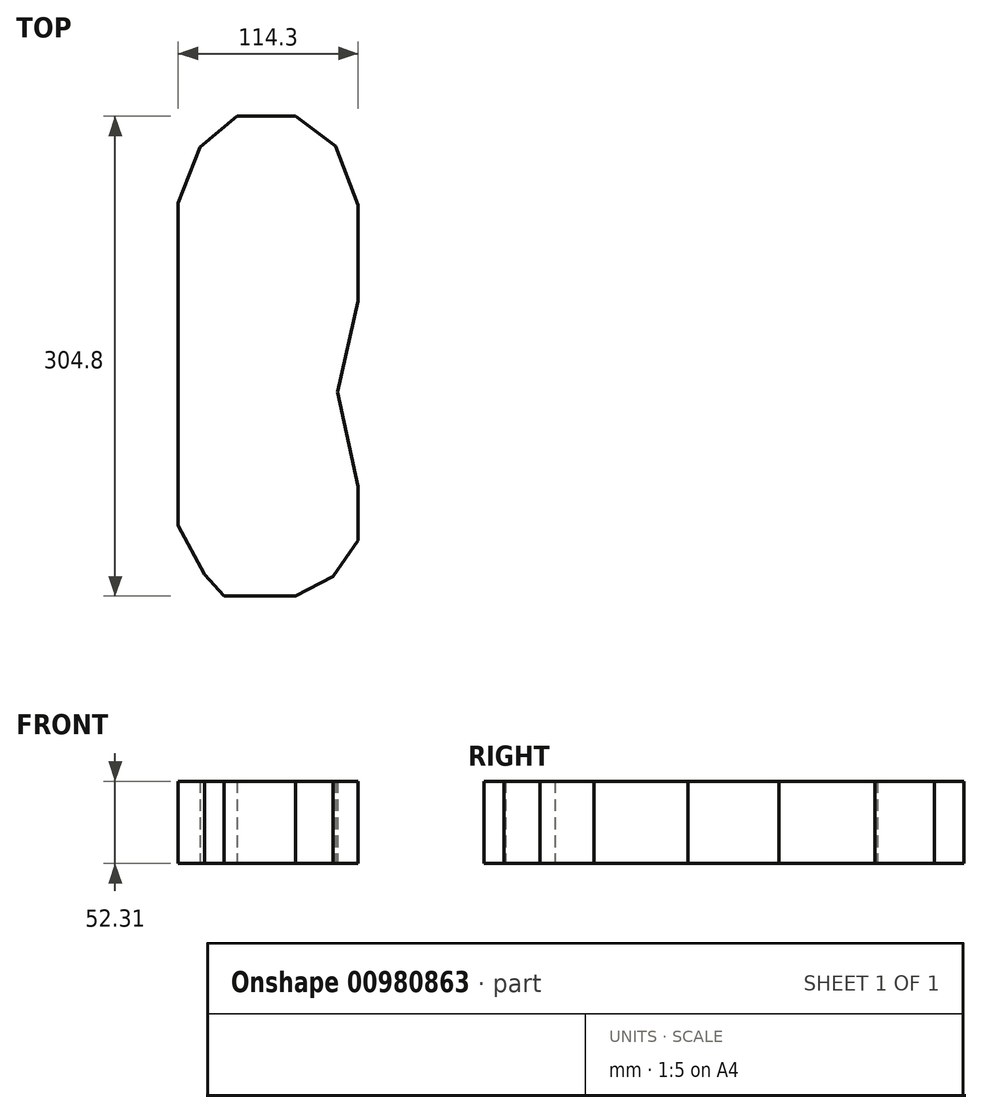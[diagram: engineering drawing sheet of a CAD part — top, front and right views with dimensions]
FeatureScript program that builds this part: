
annotation { "Feature Type Name" : "Feature", "Feature Type Description" : "" }
export const myFeature = defineFeature(function(context is Context, id is Id, definition is map)
    precondition{}
    {
        {
            var Q0;
            Q0=qCreatedBy(makeId("Top.planeOp"),FACE);
            var sketch = newSketch(context, id + "F0", { "sketchPlane" : qUnion([Q0])});
            skLineSegment(sketch, "E0", {"start": v(0, 0) * mm, "end": v(-114.3, 0) * mm});
            skLineSegment(sketch, "E1", {"start": v(-114.3, 304.8) * mm, "end": v(-114.3, 0) * mm});
            skLineSegment(sketch, "E2", {"start": v(0, 304.8) * mm, "end": v(0, 0) * mm});
            skLineSegment(sketch, "E3", {"start": v(-114.3, 304.8) * mm, "end": v(0, 304.8) * mm});
            skLineSegment(sketch, "E4", {"start": v(0, 187.34) * mm, "end": v(0, 69.7) * mm});
            skLineSegment(sketch, "E5", {"start": v(0, 248.35) * mm, "end": v(-14.43, 286.04) * mm});
            skLineSegment(sketch, "E6", {"start": v(-14.43, 286.04) * mm, "end": v(-39.67, 304.8) * mm});
            skLineSegment(sketch, "E7", {"start": v(-39.67, 304.8) * mm, "end": v(-77, 304.8) * mm});
            skLineSegment(sketch, "E8", {"start": v(-77, 304.8) * mm, "end": v(-100.47, 285.33) * mm});
            skLineSegment(sketch, "E9", {"start": v(-100.47, 285.33) * mm, "end": v(-114.3, 249.77) * mm});
            skLineSegment(sketch, "E10", {"start": v(0, 69.7) * mm, "end": v(-13, 129.59) * mm});
            skLineSegment(sketch, "E11", {"start": v(-13, 129.59) * mm, "end": v(0, 187.34) * mm});
            skLineSegment(sketch, "E12", {"start": v(0, 35.36) * mm, "end": v(-15.85, 12.6) * mm});
            skLineSegment(sketch, "E13", {"start": v(-15.85, 12.6) * mm, "end": v(-39.67, 0) * mm});
            skLineSegment(sketch, "E14", {"start": v(-39.67, 0) * mm, "end": v(-85.18, 0) * mm});
            skLineSegment(sketch, "E15", {"start": v(-85.18, 0) * mm, "end": v(-97.63, 13.68) * mm});
            skLineSegment(sketch, "E16", {"start": v(-97.63, 13.68) * mm, "end": v(-114.3, 44.97) * mm});
            skSolve(sketch);
        }
        {
            var Q0;
            {var subQ7=sQuery(id+"F0.wireOp",EDGE,"E5");Q0=makeQuery(id+"F0.imprint","IMPRINT",FACE,{"disambiguationData":[TD([[makeQuery(id+"F0.imprint","IMPRINT",EDGE,{"derivedFrom":subQ7}),1.0]])]});}
            extrude(context, id + "F1", {"entities" : qUnion([Q0]), "depth" : 52.3 * mm, "offsetDistance" : 25.4 * mm});
        }
    });
